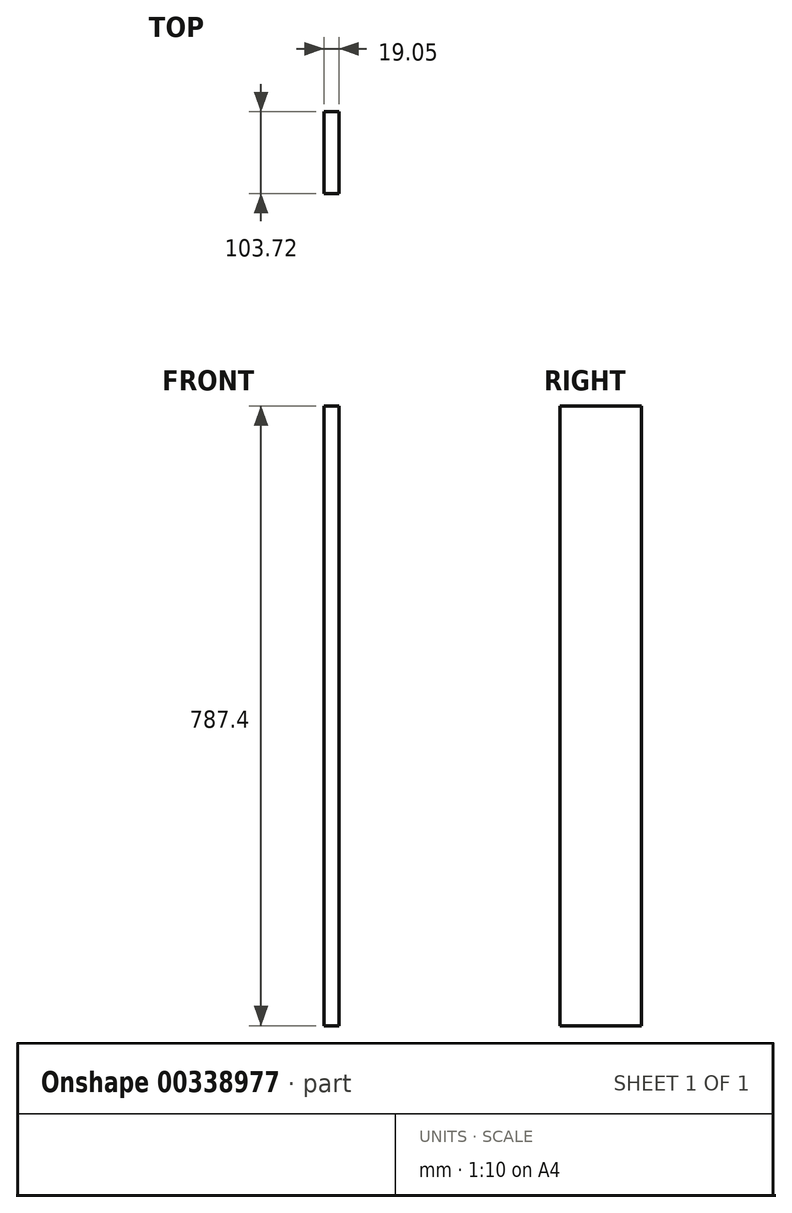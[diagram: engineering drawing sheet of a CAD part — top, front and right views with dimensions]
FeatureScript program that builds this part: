
annotation { "Feature Type Name" : "Feature", "Feature Type Description" : "" }
export const myFeature = defineFeature(function(context is Context, id is Id, definition is map)
    precondition{}
    {
        {
            var Q0;
            Q0=qCreatedBy(makeId("Right.planeOp"),FACE);
            var sketch = newSketch(context, id + "F0", { "sketchPlane" : qUnion([Q0])});
            skLineSegment(sketch, "E0.bottom", {"start": v(51.86, -393.7) * mm, "end": v(-51.86, -393.7) * mm});
            skLineSegment(sketch, "E0.top", {"start": v(51.86, 393.7) * mm, "end": v(-51.86, 393.7) * mm});
            skLineSegment(sketch, "E0.left", {"start": v(51.86, -393.7) * mm, "end": v(51.86, 393.7) * mm});
            skLineSegment(sketch, "E0.right", {"start": v(-51.86, -393.7) * mm, "end": v(-51.86, 393.7) * mm});
            skPoint(sketch, "E0.middle", {"position": v(0, 0) * mm});
            skSolve(sketch);
        }
        {
            var Q0;
            Q0 = qSketchRegion(id + "F0", true);
            extrude(context, id + "F1", {"entities" : qUnion([Q0]), "depth" : 19.05 * mm});
        }
    });
